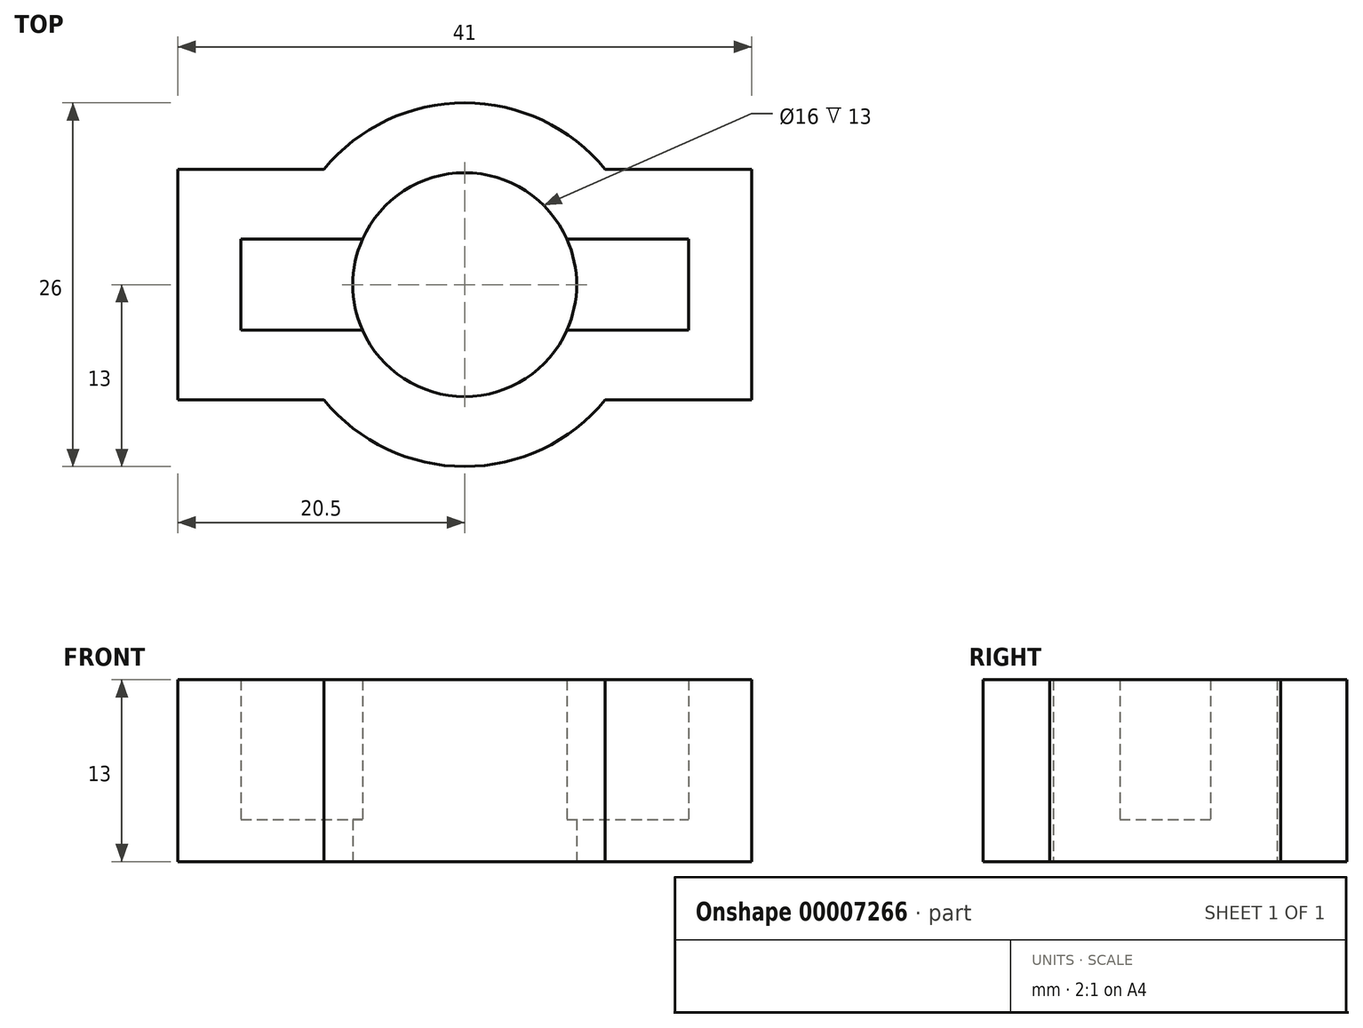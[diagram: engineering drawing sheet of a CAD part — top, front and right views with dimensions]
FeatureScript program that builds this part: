
annotation { "Feature Type Name" : "Feature", "Feature Type Description" : "" }
export const myFeature = defineFeature(function(context is Context, id is Id, definition is map)
    precondition{}
    {
        {
            var Q0;
            Q0=qCreatedBy(makeId("Top.planeOp"),FACE);
            var sketch = newSketch(context, id + "F0", { "sketchPlane" : qUnion([Q0])});
            skCircle(sketch, "E0", {"center": v(0, 0) * mm, "radius": 8 * mm});
            skArc(sketch, "E1", {"start": v(10.05, 8.25) * mm, "mid": v(0, 13) * mm, "end": v(-10.05, 8.25) * mm});
            skLineSegment(sketch, "E2.rect.bottom", {"start": v(20.5, -8.25) * mm, "end": v(10.05, -8.25) * mm});
            skLineSegment(sketch, "E2.rect.top", {"start": v(20.5, 8.25) * mm, "end": v(10.05, 8.25) * mm});
            skLineSegment(sketch, "E2.rect.left", {"start": v(20.5, -8.25) * mm, "end": v(20.5, 8.25) * mm});
            skLineSegment(sketch, "E2.rect.right", {"start": v(-20.5, -8.25) * mm, "end": v(-20.5, 8.25) * mm});
            skLineSegment(sketch, "E3.trimOffspring", {"start": v(-10.05, 8.25) * mm, "end": v(-20.5, 8.25) * mm});
            skLineSegment(sketch, "E4.trimOffspring", {"start": v(-10.05, -8.25) * mm, "end": v(-20.5, -8.25) * mm});
            skArc(sketch, "E5.trimOffspring", {"start": v(-10.05, -8.25) * mm, "mid": v(0, -13) * mm, "end": v(10.05, -8.25) * mm});
            skSolve(sketch);
        }
        {
            var Q0;
            Q0 = qSketchRegion(id + "F0", true);
            extrude(context, id + "F1", {"entities" : qUnion([Q0]), "depth" : 3 * mm});
        }
        {
            var Q0;
            Q0=makeQuery(id+"F1.opExtrude","CAP_FACE",FACE,{"disambiguationData":[OSD([sQuery(id+"F0.wireOp",EDGE,"E0"),sQuery(id+"F0.wireOp",EDGE,"E1"),sQuery(id+"F0.wireOp",EDGE,"E2.rect.bottom"),sQuery(id+"F0.wireOp",EDGE,"E2.rect.top"),sQuery(id+"F0.wireOp",EDGE,"E2.rect.left"),sQuery(id+"F0.wireOp",EDGE,"E2.rect.right"),sQuery(id+"F0.wireOp",EDGE,"E3.trimOffspring"),sQuery(id+"F0.wireOp",EDGE,"E4.trimOffspring"),sQuery(id+"F0.wireOp",EDGE,"E5.trimOffspring")])],"isStart":false});
            var sketch = newSketch(context, id + "F2", { "sketchPlane" : qUnion([Q0])});
            skArc(sketch, "E6.0", {"start": v(10.05, 8.25) * mm, "mid": v(0, 13) * mm, "end": v(-10.05, 8.25) * mm});
            skLineSegment(sketch, "E6.1", {"start": v(20.5, 8.25) * mm, "end": v(10.05, 8.25) * mm});
            skLineSegment(sketch, "E6.2", {"start": v(20.5, -8.25) * mm, "end": v(20.5, 8.25) * mm});
            skLineSegment(sketch, "E6.3", {"start": v(20.5, -8.25) * mm, "end": v(10.05, -8.25) * mm});
            skArc(sketch, "E6.4", {"start": v(-10.05, -8.25) * mm, "mid": v(0, -13) * mm, "end": v(10.05, -8.25) * mm});
            skLineSegment(sketch, "E6.5", {"start": v(-10.05, -8.25) * mm, "end": v(-20.5, -8.25) * mm});
            skLineSegment(sketch, "E6.6", {"start": v(-20.5, -8.25) * mm, "end": v(-20.5, 8.25) * mm});
            skLineSegment(sketch, "E6.7", {"start": v(-10.05, 8.25) * mm, "end": v(-20.5, 8.25) * mm});
            skLineSegment(sketch, "E7", {"start": v(-16, 3.25) * mm, "end": v(-16, -3.25) * mm});
            skLineSegment(sketch, "E8", {"start": v(-16, -3.25) * mm, "end": v(-7.31, -3.25) * mm});
            skLineSegment(sketch, "E9", {"start": v(7.31, -3.25) * mm, "end": v(16, -3.25) * mm});
            skLineSegment(sketch, "E10", {"start": v(16, -3.25) * mm, "end": v(16, 3.25) * mm});
            skLineSegment(sketch, "E11", {"start": v(16, 3.25) * mm, "end": v(7.31, 3.25) * mm});
            skLineSegment(sketch, "E12", {"start": v(-16, 3.25) * mm, "end": v(-7.31, 3.25) * mm});
            skArc(sketch, "E13.0", {"start": v(-7.31, -3.25) * mm, "mid": v(0, -8) * mm, "end": v(7.31, -3.25) * mm});
            skArc(sketch, "E14.trimOffspring", {"start": v(7.31, 3.25) * mm, "mid": v(0, 8) * mm, "end": v(-7.31, 3.25) * mm});
            skSolve(sketch);
        }
        {
            var Q0;
            Q0 = qSketchRegion(id + "F2", true);
            extrude(context, id + "F3", {"entities" : qUnion([Q0]), "operationType" : NewBodyOperationType.ADD, "depth" : 10 * mm});
        }
    });
